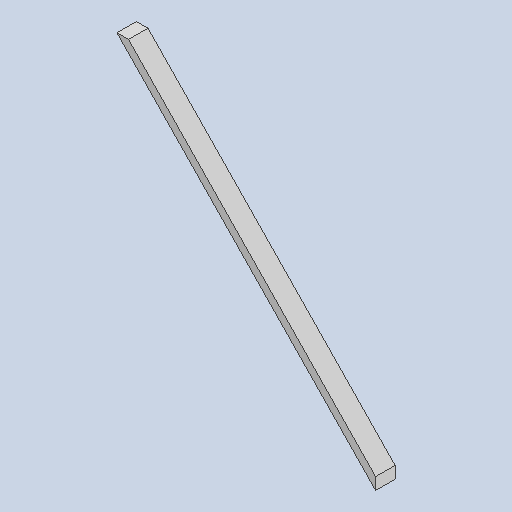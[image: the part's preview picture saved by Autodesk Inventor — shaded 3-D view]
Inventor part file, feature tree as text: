
AUTODESK INVENTOR PART (.ipt)
format: ipt  version: 2025 (Build 290162000, 162)  size: 78,848 bytes
history: native  units: in
note: dims shown in document units (in); Inventor stores cm internally (conversion verified against a paired STEP export)
features: other x3, sketch x1
ambient origin geometry x8: Origin, YZ Plane, XZ Plane, XY Plane, X Axis, Y Axis, Z Axis, Center Point
bodies: Solid1 (feature_tree)
feature tree (4):
  other  "side-side.ipt"
  other  "Solid1::side-side.ipt"
  other  "TaggingFeature1"
  sketch  "Sketch1"  dims[d0=0.3937in]
